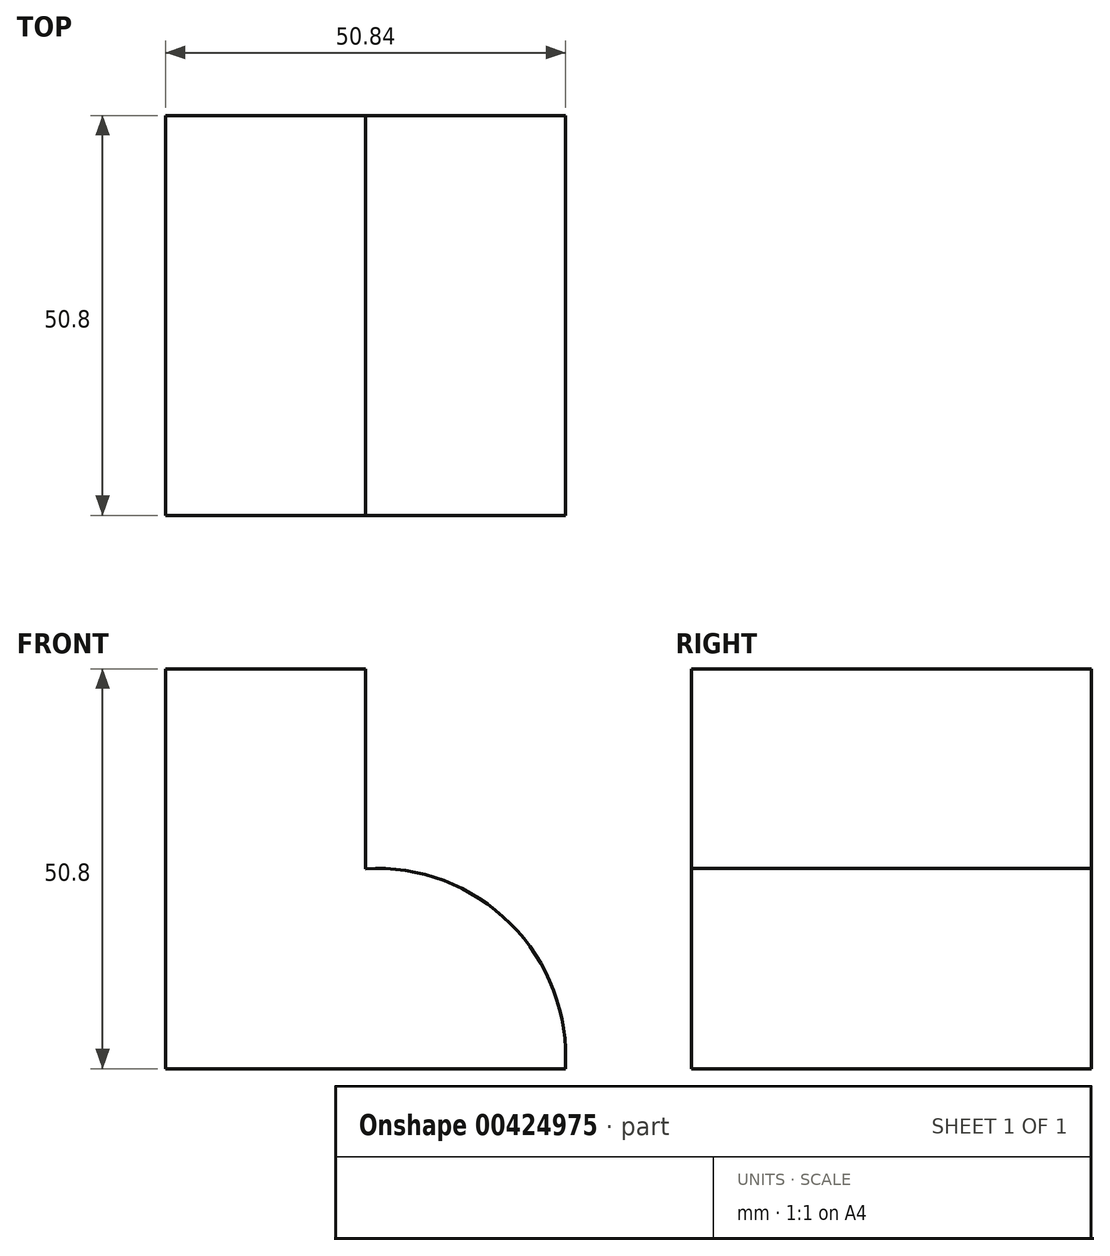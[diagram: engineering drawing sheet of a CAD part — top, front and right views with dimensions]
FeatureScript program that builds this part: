
annotation { "Feature Type Name" : "Feature", "Feature Type Description" : "" }
export const myFeature = defineFeature(function(context is Context, id is Id, definition is map)
    precondition{}
    {
        {
            var Q0;
            Q0=qCreatedBy(makeId("Front.planeOp"),FACE);
            var sketch = newSketch(context, id + "F0", { "sketchPlane" : qUnion([Q0])});
            skLineSegment(sketch, "E0", {"start": v(0, 0) * mm, "end": v(-50.8, 0) * mm});
            skLineSegment(sketch, "E1", {"start": v(-50.8, 0) * mm, "end": v(-50.8, 50.8) * mm});
            skLineSegment(sketch, "E2", {"start": v(-50.8, 50.8) * mm, "end": v(-25.4, 50.8) * mm});
            skLineSegment(sketch, "E3", {"start": v(-25.4, 50.8) * mm, "end": v(-25.4, 25.4) * mm});
            skArc(sketch, "E4", {"start": v(0, 0) * mm, "mid": v(-6.98, 18.42) * mm, "end": v(-25.4, 25.4) * mm});
            skSolve(sketch);
        }
        {
            var Q0;
            Q0 = qSketchRegion(id + "F0", true);
            extrude(context, id + "F1", {"entities" : qUnion([Q0]), "depth" : 50.8 * mm});
        }
    });
